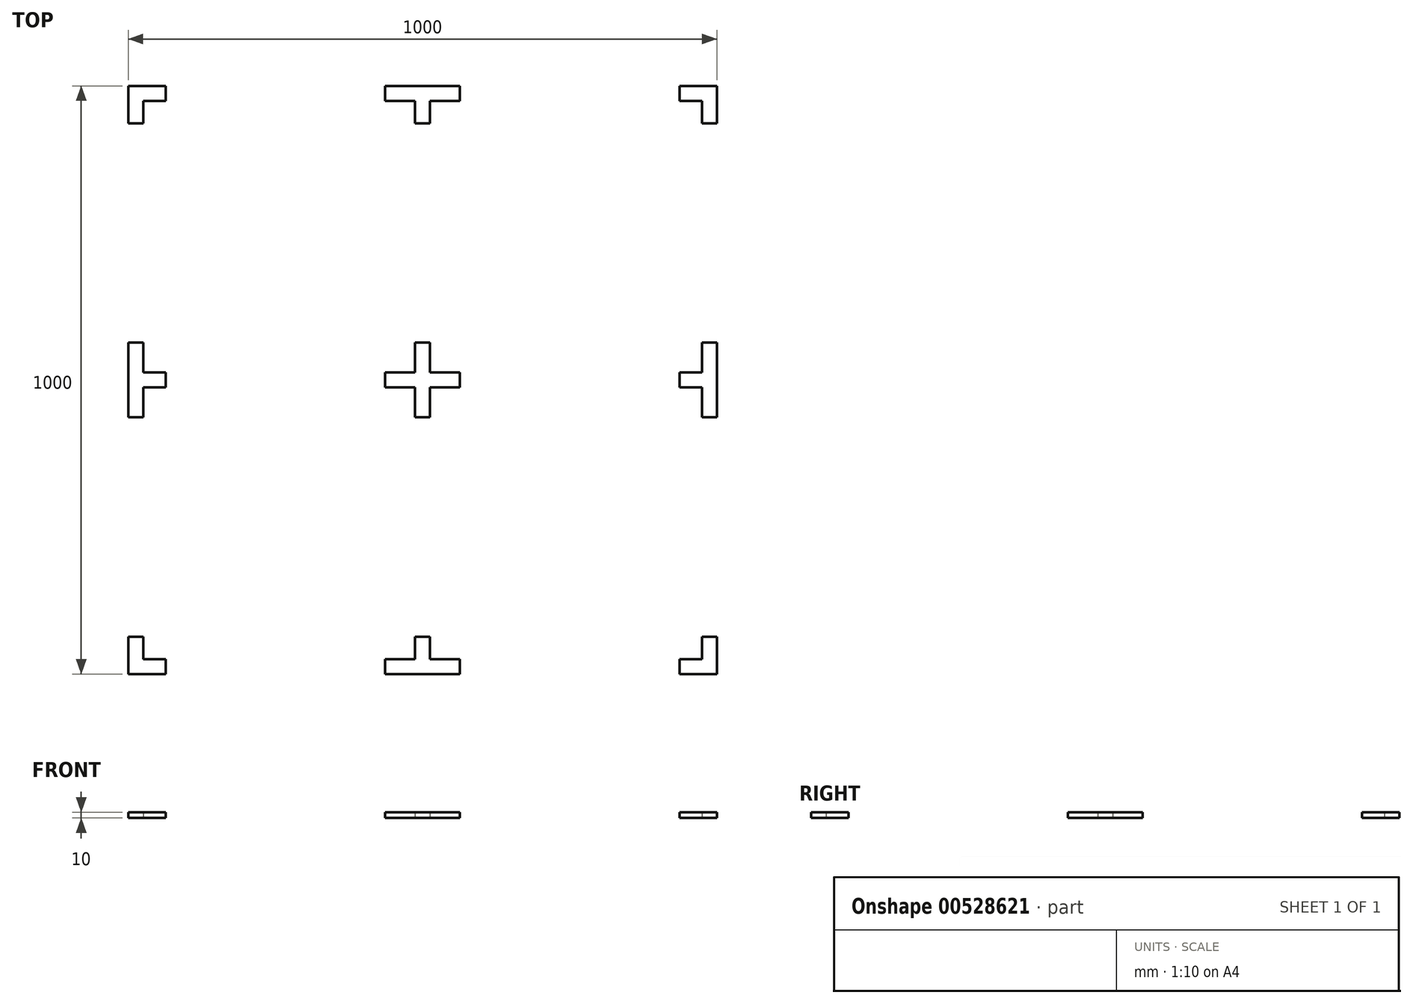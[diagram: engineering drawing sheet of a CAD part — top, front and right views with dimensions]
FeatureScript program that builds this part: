
annotation { "Feature Type Name" : "Feature", "Feature Type Description" : "" }
export const myFeature = defineFeature(function(context is Context, id is Id, definition is map)
    precondition{}
    {
        {
            var Q0;
            Q0=qCreatedBy(makeId("Top.planeOp"),FACE);
            var sketch = newSketch(context, id + "F0", { "sketchPlane" : qUnion([Q0])});
            skLineSegment(sketch, "E0.bottom", {"start": v(-500, 500) * mm, "end": v(-436.5, 500) * mm});
            skLineSegment(sketch, "E0.top", {"start": v(-500, -500) * mm, "end": v(-436.5, -500) * mm});
            skLineSegment(sketch, "E0.left", {"start": v(-500, 500) * mm, "end": v(-500, 436.5) * mm});
            skLineSegment(sketch, "E0.right", {"start": v(500, 500) * mm, "end": v(500, 436.5) * mm});
            skPoint(sketch, "E0.middle", {"position": v(0, 0) * mm});
            skLineSegment(sketch, "E1.0", {"start": v(-474.6, -474.6) * mm, "end": v(-436.5, -474.6) * mm});
            skLineSegment(sketch, "E1.1", {"start": v(-474.6, 474.6) * mm, "end": v(-474.6, 436.5) * mm});
            skLineSegment(sketch, "E1.2", {"start": v(-474.6, 474.6) * mm, "end": v(-436.5, 474.6) * mm});
            skLineSegment(sketch, "E1.3", {"start": v(474.6, 474.6) * mm, "end": v(474.6, 436.5) * mm});
            skLineSegment(sketch, "E2.bottom", {"start": v(63.5, 12.7) * mm, "end": v(12.7, 12.7) * mm});
            skLineSegment(sketch, "E2.top", {"start": v(63.5, -12.7) * mm, "end": v(12.7, -12.7) * mm});
            skLineSegment(sketch, "E2.left", {"start": v(63.5, 12.7) * mm, "end": v(63.5, -12.7) * mm});
            skLineSegment(sketch, "E2.right", {"start": v(-63.5, 12.7) * mm, "end": v(-63.5, -12.7) * mm});
            skLineSegment(sketch, "E3.bottom", {"start": v(-12.7, 63.5) * mm, "end": v(12.7, 63.5) * mm});
            skLineSegment(sketch, "E3.top", {"start": v(-12.7, -63.5) * mm, "end": v(12.7, -63.5) * mm});
            skLineSegment(sketch, "E3.left", {"start": v(-12.7, 63.5) * mm, "end": v(-12.7, 12.7) * mm});
            skLineSegment(sketch, "E3.right", {"start": v(12.7, 63.5) * mm, "end": v(12.7, 12.7) * mm});
            skLineSegment(sketch, "E4.trimOffspring", {"start": v(-12.7, -12.7) * mm, "end": v(-12.7, -63.5) * mm});
            skLineSegment(sketch, "E5.trimOffspring", {"start": v(-12.7, -12.7) * mm, "end": v(-63.5, -12.7) * mm});
            skLineSegment(sketch, "E6.trimOffspring", {"start": v(12.7, -12.7) * mm, "end": v(12.7, -63.5) * mm});
            skLineSegment(sketch, "E7.trimOffspring", {"start": v(-12.7, 12.7) * mm, "end": v(-63.5, 12.7) * mm});
            skLineSegment(sketch, "E8", {"start": v(-12.7, 474.6) * mm, "end": v(-12.7, 436.5) * mm});
            skLineSegment(sketch, "E9", {"start": v(-12.7, 436.5) * mm, "end": v(12.7, 436.5) * mm});
            skLineSegment(sketch, "E10", {"start": v(12.7, 436.5) * mm, "end": v(12.7, 474.6) * mm});
            skLineSegment(sketch, "E11.trimOffspring", {"start": v(12.7, 474.6) * mm, "end": v(63.5, 474.6) * mm});
            skLineSegment(sketch, "E12", {"start": v(0, 436.5) * mm, "end": v(0, 500) * mm, "construction": true});
            skLineSegment(sketch, "E13", {"start": v(-63.5, 474.6) * mm, "end": v(-63.5, 500) * mm});
            skLineSegment(sketch, "E14", {"start": v(63.5, 474.6) * mm, "end": v(63.5, 500) * mm});
            skLineSegment(sketch, "E15", {"start": v(-436.5, 474.6) * mm, "end": v(-436.5, 500) * mm});
            skLineSegment(sketch, "E16", {"start": v(-474.6, 436.5) * mm, "end": v(-500, 436.5) * mm});
            skLineSegment(sketch, "E17.trimOffspring", {"start": v(-63.5, 500) * mm, "end": v(63.5, 500) * mm});
            skLineSegment(sketch, "E18.trimOffspring", {"start": v(-63.5, 474.6) * mm, "end": v(-12.7, 474.6) * mm});
            skLineSegment(sketch, "E19", {"start": v(436.5, 474.6) * mm, "end": v(436.5, 500) * mm});
            skLineSegment(sketch, "E20", {"start": v(474.6, 436.5) * mm, "end": v(500, 436.5) * mm});
            skLineSegment(sketch, "E21.trimOffspring", {"start": v(436.5, 500) * mm, "end": v(500, 500) * mm});
            skLineSegment(sketch, "E22.trimOffspring", {"start": v(436.5, 474.6) * mm, "end": v(474.6, 474.6) * mm});
            skLineSegment(sketch, "E23", {"start": v(-500, -436.5) * mm, "end": v(-474.6, -436.5) * mm});
            skLineSegment(sketch, "E24", {"start": v(-436.5, -474.6) * mm, "end": v(-436.5, -500) * mm});
            skLineSegment(sketch, "E25", {"start": v(-500, -63.5) * mm, "end": v(-474.6, -63.5) * mm});
            skLineSegment(sketch, "E26", {"start": v(-500, 63.5) * mm, "end": v(-474.6, 63.5) * mm});
            skLineSegment(sketch, "E27", {"start": v(-474.6, 12.7) * mm, "end": v(-436.5, 12.7) * mm});
            skLineSegment(sketch, "E28", {"start": v(-436.5, 12.7) * mm, "end": v(-436.5, -12.7) * mm});
            skLineSegment(sketch, "E29", {"start": v(-436.5, -12.7) * mm, "end": v(-474.6, -12.7) * mm});
            skLineSegment(sketch, "E30", {"start": v(-436.5, 0) * mm, "end": v(-500, 0) * mm, "construction": true});
            skLineSegment(sketch, "E31.trimOffspring", {"start": v(-500, 63.5) * mm, "end": v(-500, -63.5) * mm});
            skLineSegment(sketch, "E32.trimOffspring", {"start": v(-474.6, 63.5) * mm, "end": v(-474.6, 12.7) * mm});
            skLineSegment(sketch, "E33.trimOffspring", {"start": v(-474.6, -12.7) * mm, "end": v(-474.6, -63.5) * mm});
            skLineSegment(sketch, "E34.trimOffspring", {"start": v(-500, -436.5) * mm, "end": v(-500, -500) * mm});
            skLineSegment(sketch, "E35.trimOffspring", {"start": v(-474.6, -436.5) * mm, "end": v(-474.6, -474.6) * mm});
            skPoint(sketch, "E36.orphan", {"position": v(500, -500) * mm});
            skLineSegment(sketch, "E37.MirrorCS", {"start": v(500, -63.5) * mm, "end": v(474.6, -63.5) * mm});
            skLineSegment(sketch, "E38.MirrorCS", {"start": v(436.5, 12.7) * mm, "end": v(436.5, -12.7) * mm});
            skLineSegment(sketch, "E39.MirrorCS", {"start": v(500, 63.5) * mm, "end": v(474.6, 63.5) * mm});
            skLineSegment(sketch, "E40.MirrorCS", {"start": v(436.5, 0) * mm, "end": v(500, 0) * mm, "construction": true});
            skLineSegment(sketch, "E41.MirrorCS", {"start": v(436.5, -12.7) * mm, "end": v(474.6, -12.7) * mm});
            skLineSegment(sketch, "E42.MirrorCS", {"start": v(474.6, 63.5) * mm, "end": v(474.6, 12.7) * mm});
            skLineSegment(sketch, "E43.MirrorCS", {"start": v(474.6, 12.7) * mm, "end": v(436.5, 12.7) * mm});
            skLineSegment(sketch, "E44.MirrorCS", {"start": v(474.6, -12.7) * mm, "end": v(474.6, -63.5) * mm});
            skLineSegment(sketch, "E45.MirrorCS", {"start": v(500, 63.5) * mm, "end": v(500, -63.5) * mm});
            skLineSegment(sketch, "E46.MirrorCS", {"start": v(12.7, -436.5) * mm, "end": v(12.7, -474.6) * mm});
            skLineSegment(sketch, "E47.MirrorCS", {"start": v(-63.5, -474.6) * mm, "end": v(-63.5, -500) * mm});
            skLineSegment(sketch, "E48.MirrorCS", {"start": v(-12.7, -436.5) * mm, "end": v(12.7, -436.5) * mm});
            skLineSegment(sketch, "E49.MirrorCS", {"start": v(-12.7, -474.6) * mm, "end": v(-12.7, -436.5) * mm});
            skLineSegment(sketch, "E50.MirrorCS", {"start": v(63.5, -474.6) * mm, "end": v(63.5, -500) * mm});
            skLineSegment(sketch, "E51.MirrorCS", {"start": v(0, -436.5) * mm, "end": v(0, -500) * mm, "construction": true});
            skLineSegment(sketch, "E52.MirrorCS", {"start": v(-63.5, -474.6) * mm, "end": v(-12.7, -474.6) * mm});
            skLineSegment(sketch, "E53.MirrorCS", {"start": v(-63.5, -500) * mm, "end": v(63.5, -500) * mm});
            skLineSegment(sketch, "E54.MirrorCS", {"start": v(12.7, -474.6) * mm, "end": v(63.5, -474.6) * mm});
            skLineSegment(sketch, "E55.MirrorCS", {"start": v(436.5, -474.6) * mm, "end": v(436.5, -500) * mm});
            skLineSegment(sketch, "E56.MirrorCS", {"start": v(474.6, -436.5) * mm, "end": v(500, -436.5) * mm});
            skLineSegment(sketch, "E57.MirrorCS", {"start": v(474.6, -474.6) * mm, "end": v(474.6, -436.5) * mm});
            skLineSegment(sketch, "E58.MirrorCS", {"start": v(436.5, -474.6) * mm, "end": v(474.6, -474.6) * mm});
            skLineSegment(sketch, "E59.MirrorCS", {"start": v(436.5, -500) * mm, "end": v(500, -500) * mm});
            skLineSegment(sketch, "E60.MirrorCS", {"start": v(500, -500) * mm, "end": v(500, -436.5) * mm});
            skSolve(sketch);
        }
        {
            var Q0;
            Q0 = qSketchRegion(id + "F0", true);
            extrude(context, id + "F1", {"entities" : qUnion([Q0]), "depth" : 10 * mm, "offsetDistance" : 25.4 * mm});
        }
    });
